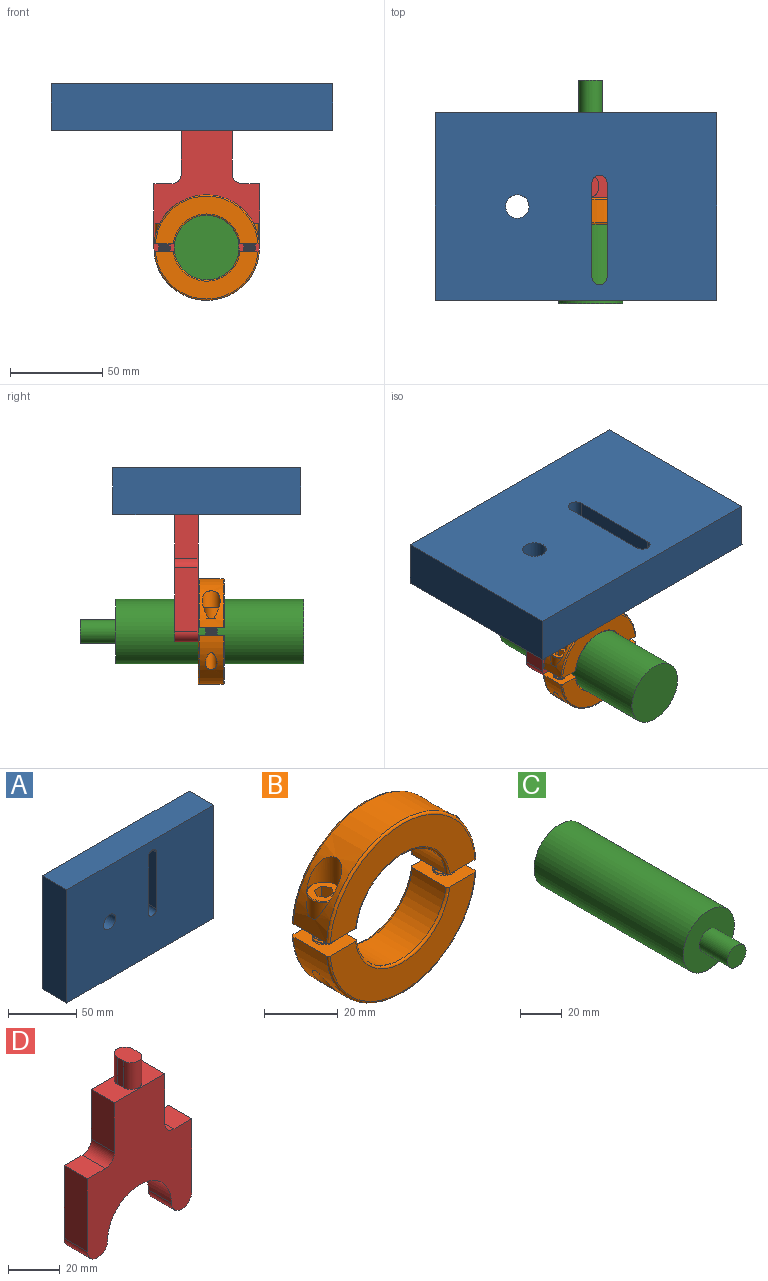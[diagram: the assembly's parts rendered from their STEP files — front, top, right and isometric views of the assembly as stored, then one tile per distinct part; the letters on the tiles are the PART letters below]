
ASSEMBLY  parts=4 mates=4
PART A: 11 faces, bbox 152.4x25.4x101.6 mm
  f0: plane 101.6x25.4mm, normal (1,0,0), area 2580.6mm2, adj f1,f3,f5,f6
  f1: plane 152.4x25.4mm, normal (0,0,1), area 3871mm2, adj f0,f2,f5,f6
  f2: plane 101.6x25.4mm, normal (-1,0,0), area 2580.6mm2, adj f1,f3,f5,f6
  f3: plane 152.4x25.4mm, normal (0,0,-1), area 3871mm2, adj f0,f2,f5,f6
  f4: cylinder r=6.35mm len=25.4mm, axis (0,1,0), area 1013.4mm2, adj f5,f6
  f5: plane 152.4x101.6mm, normal (0,-1,0), area 14884.3mm2, adj f0,f1,f2,f3,f4,f7,f8,f9
  f6: plane 152.4x101.6mm, normal (0,1,0), area 14884.3mm2, adj f0,f1,f2,f3,f4,f7,f8,f9
  f7: cylinder r=4.13mm len=25.4mm, axis (0,-1,0), area 329.4mm2, adj f5,f6,f8,f9
  f8: plane 50.8x25.4mm, normal (-1,0,0), area 1290.3mm2, adj f5,f6,f7,f10
  f9: plane 50.8x25.4mm, normal (1,0,0), area 1290.3mm2, adj f5,f6,f7,f10
  f10: cylinder r=4.13mm len=25.4mm, axis (0,-1,0), area 329.4mm2, adj f5,f6,f8,f9
PART B: 81 faces, bbox 62x14.8x62.2 mm
  f0: plane 1.42x0.05mm, normal (0,0,-1), area 0.1mm2, adj f2,f35
  f1: plane 9.02x9.02mm, normal (0,0,1), area 44.2mm2, adj f3,f4,f5,f6,f7,f8,f10
  f2: cylinder r=4.76mm len=9.53mm, axis (0,0,-1), area 182.4mm2, adj f0,f10,f11
  f3: plane 4.76x2.75mm, normal (0,1,0), area 13.1mm2, adj f1,f4,f8,f9
  f4: plane 4.76x2.38mm, normal (0.87,0.5,0), area 13.1mm2, adj f1,f3,f5,f9
  f5: plane 4.76x2.38mm, normal (0.87,-0.5,0), area 13.1mm2, adj f1,f4,f6,f9
  f6: plane 4.76x2.75mm, normal (0,-1,0), area 13.1mm2, adj f1,f5,f7,f9
  f7: plane 4.76x2.38mm, normal (-0.87,-0.5,0), area 13.1mm2, adj f1,f6,f8,f9
  f8: plane 4.76x2.38mm, normal (-0.87,0.5,0), area 13.1mm2, adj f1,f3,f7,f9
  f9: plane 5.5x4.76mm, normal (0,0,1), area 19.6mm2, adj f3,f4,f5,f6,f7,f8
  f10: cone r=4.76mm half-angle=45deg, axis (0,0,-1), area 10.5mm2, adj f1,f2
  f11: plane 9.65x9.54mm, normal (0,0,1), area 1.8mm2, adj f2,f35,f47
  f12: cylinder r=3.17mm len=6.35mm, axis (0,0,-1), area 83.1mm2, adj f38,f77,f79,f80
  f13: cylinder r=3.17mm len=13.63mm, axis (0,0,1), area 180.7mm2, adj f19,f63,f78,f79,f80
  f14: cylinder r=3.17mm len=6.35mm, axis (0,0,1), area 11.1mm2, adj f15,f20,f64,f79,f80
  f15: cylinder r=3.17mm len=6.35mm, axis (0,0,1), area 15.8mm2, adj f14,f16,f79,f80
  f16: cylinder r=3.17mm len=6.35mm, axis (0,0,1), area 15.8mm2, adj f15,f17,f79,f80
  f17: cylinder r=3.17mm len=6.35mm, axis (0,0,1), area 15.8mm2, adj f16,f18,f79,f80
  f18: cylinder r=3.17mm len=6.35mm, axis (0,0,1), area 15.8mm2, adj f17,f19,f79,f80
  f19: cylinder r=3.17mm len=6.35mm, axis (0,0,1), area 15.8mm2, adj f13,f18,f79,f80
  f20: cylinder r=3.17mm len=2.58mm, axis (0,0,1), area 0.2mm2, adj f14,f64,f80
  f21: plane 9.02x9.02mm, normal (0,0,1), area 44.2mm2, adj f24,f25,f26,f27,f28,f29,f31
  f22: cylinder r=4.76mm len=9.53mm, axis (0,0,-1), area 182.4mm2, adj f23,f31,f32
  f23: plane 1.42x0.05mm, normal (0,0,-1), area 0.1mm2, adj f22,f35
  f24: plane 4.76x2.75mm, normal (0,1,0), area 13.1mm2, adj f21,f25,f29,f30
  f25: plane 4.76x2.38mm, normal (0.87,0.5,0), area 13.1mm2, adj f21,f24,f26,f30
  f26: plane 4.76x2.38mm, normal (0.87,-0.5,0), area 13.1mm2, adj f21,f25,f27,f30
  f27: plane 4.76x2.75mm, normal (0,-1,0), area 13.1mm2, adj f21,f26,f28,f30
  f28: plane 4.76x2.38mm, normal (-0.87,-0.5,0), area 13.1mm2, adj f21,f27,f29,f30
  f29: plane 4.76x2.38mm, normal (-0.87,0.5,0), area 13.1mm2, adj f21,f24,f28,f30
  f30: plane 5.5x4.76mm, normal (0,0,1), area 19.6mm2, adj f24,f25,f26,f27,f28,f29
  f31: cone r=4.76mm half-angle=45deg, axis (0,0,-1), area 10.5mm2, adj f21,f22
  f32: plane 9.65x9.54mm, normal (0,0,1), area 1.8mm2, adj f22,f35,f46
  f33: cylinder r=3.17mm len=6.35mm, axis (0,0,-1), area 83.1mm2, adj f36,f52,f53,f54
  f34: plane 55.56x25.72mm, normal (0,1,0), area 353.2mm2, adj f36,f38,f41,f45
  f35: cylinder r=28.57mm len=56.99mm, axis (0,1,0), area 828.9mm2, adj f0,f11,f23,f32,f36,f38,f41,f42
  f36: plane 14.32x11.2mm, normal (0,0,-1), area 127.3mm2, adj f33,f34,f35,f37,f39,f40,f41,f42
  f37: cylinder r=17.46mm len=34.66mm, axis (0,1,0), area 650.2mm2, adj f36,f38,f43,f44
  f38: plane 14.32x11.2mm, normal (0,0,-1), area 127.3mm2, adj f12,f34,f35,f37,f39,f40,f41,f42
  f39: plane 55.56x25.72mm, normal (0,-1,0), area 658.7mm2, adj f36,f38,f42,f43
  f40: plane 45.46x20.69mm, normal (0,1,0), area 279.6mm2, adj f36,f38,f44,f45
  f41: torus R=27.86mm, axis (0,-1,0), area 95mm2, adj f34,f35,f36,f38
  f42: torus R=27.86mm, axis (0,-1,0), area 95mm2, adj f35,f36,f38,f39
  f43: torus R=18.18mm, axis (0,-1,0), area 57.7mm2, adj f36,f37,f38,f39
  f44: torus R=18.18mm, axis (0,-1,0), area 57.7mm2, adj f36,f37,f38,f40
  f45: torus R=23.02mm, axis (0,1,0), area 40.7mm2, adj f34,f36,f38,f40
  f46: cylinder r=4.83mm len=15.13mm, axis (0,0,-1), area 267.6mm2, adj f32,f35
  f47: cylinder r=4.83mm len=15.13mm, axis (0,0,-1), area 267.5mm2, adj f11,f35
  f48: plane 4.54x4.54mm, normal (0,0,-1), area 16.2mm2, adj f49
  f49: cone r=2.27mm half-angle=45deg, axis (0,0,1), area 14.2mm2, adj f48,f50,f53,f54,f55
  f50: cylinder r=2.59mm len=15.56mm, axis (0,0,-1), area 31.4mm2, adj f49,f52,f53,f54
  f51: cylinder r=3.17mm len=6.35mm, axis (0,0,-1), area 10.6mm2, adj f36,f53,f54,f66
  f52: plane 6.71x6.7mm, normal (0,0,-1), area 5.5mm2, adj f33,f50,f53,f54
  f53: bspline ~16.02x6.45mm, area 207.1mm2, adj f33,f49,f50,f51,f52,f55,f56,f57
  f54: bspline ~16.47x6.45mm, area 206.6mm2, adj f33,f49,f50,f51,f52,f55,f56,f57
  f55: cylinder r=3.17mm len=14.09mm, axis (0,0,-1), area 188.6mm2, adj f49,f53,f54,f60,f63
  f56: cylinder r=3.17mm len=6.35mm, axis (0,0,-1), area 15.4mm2, adj f53,f54,f57,f61,f66
  f57: cylinder r=3.17mm len=6.35mm, axis (0,0,-1), area 15.8mm2, adj f53,f54,f56,f58
  f58: cylinder r=3.17mm len=6.35mm, axis (0,0,-1), area 15.8mm2, adj f53,f54,f57,f59
  f59: cylinder r=3.17mm len=6.35mm, axis (0,0,-1), area 15.8mm2, adj f53,f54,f58,f60
  f60: cylinder r=3.17mm len=6.35mm, axis (0,0,-1), area 15.8mm2, adj f53,f54,f55,f59
  f61: cylinder r=3.17mm len=6.35mm, axis (0,0,-1), area 3.8mm2, adj f54,f56,f66
  f62: plane 55.56x25.72mm, normal (0,1,0), area 353.2mm2, adj f64,f66,f72,f73
  f63: cylinder r=28.57mm len=56.99mm, axis (0,1,0), area 988.8mm2, adj f13,f55,f64,f66,f69,f72
  f64: plane 14.32x11.2mm, normal (0,0,1), area 127.3mm2, adj f14,f20,f62,f63,f65,f67,f68,f69
  f65: cylinder r=17.46mm len=34.66mm, axis (0,1,0), area 650.2mm2, adj f64,f66,f70,f71
  f66: plane 14.32x11.2mm, normal (0,0,1), area 127.3mm2, adj f51,f56,f61,f62,f63,f65,f67,f68
  f67: plane 55.56x25.72mm, normal (0,-1,0), area 658.7mm2, adj f64,f66,f69,f70
  f68: plane 45.46x20.69mm, normal (0,1,0), area 279.6mm2, adj f64,f66,f71,f73
  f69: torus R=27.86mm, axis (0,-1,0), area 95mm2, adj f63,f64,f66,f67
  f70: torus R=18.18mm, axis (0,-1,0), area 57.7mm2, adj f64,f65,f66,f67
  f71: torus R=18.18mm, axis (0,-1,0), area 57.7mm2, adj f64,f65,f66,f68
  f72: torus R=27.86mm, axis (0,-1,0), area 95mm2, adj f62,f63,f64,f66
  f73: torus R=23.02mm, axis (0,1,0), area 40.7mm2, adj f62,f64,f66,f68
  f74: plane 4.54x4.54mm, normal (0,0,-1), area 16.2mm2, adj f78
  f75: cylinder r=2.59mm len=15.56mm, axis (0,0,-1), area 31.4mm2, adj f77,f78,f79,f80
  f76: cylinder r=3.17mm len=6.35mm, axis (0,0,-1), area 10.6mm2, adj f38,f64,f79,f80
  f77: plane 6.71x6.7mm, normal (0,0,-1), area 5.5mm2, adj f12,f75,f79,f80
  f78: cone r=2.27mm half-angle=45deg, axis (0,0,1), area 14.2mm2, adj f13,f74,f75,f79,f80
  f79: bspline ~16.02x6.45mm, area 207.1mm2, adj f12,f13,f14,f15,f16,f17,f18,f19
  f80: bspline ~16.47x6.45mm, area 206.6mm2, adj f12,f13,f14,f15,f16,f17,f18,f19
PART C: 5 faces, bbox 34.9x120.7x34.9 mm
  f0: cylinder r=17.46mm len=101.6mm, axis (0,1,0), area 11147.6mm2, adj f1,f3
  f1: plane 34.93x34.93mm, normal (0,1,0), area 958mm2, adj f0
  f2: cylinder r=6.35mm len=19.05mm, axis (0,-1,0), area 760.1mm2, adj f3,f4
  f3: plane 34.93x34.93mm, normal (0,-1,0), area 831.3mm2, adj f0,f2
  f4: plane 12.7x12.7mm, normal (0,-1,0), area 126.7mm2, adj f2
PART D: 19 faces, bbox 57.2x12.7x81.5 mm
  f0: plane 68.84x57.15mm, normal (0,1,0), area 2396.2mm2, adj f1,f2,f3,f4,f5,f6,f7,f8
  f1: cylinder r=5.56mm len=12.7mm, axis (0,1,0), area 221.7mm2, adj f0,f2,f9,f10
  f2: plane 34.6x12.7mm, normal (1,0,0), area 439.4mm2, adj f0,f1,f3,f10
  f3: plane 12.7x9.73mm, normal (0,0,1), area 123.5mm2, adj f0,f2,f10,f11
  f4: plane 23.61x12.7mm, normal (1,0,0), area 299.9mm2, adj f0,f10,f11,f13
  f5: plane 23.61x12.7mm, normal (-1,0,0), area 299.9mm2, adj f0,f10,f12,f13
  f6: plane 12.7x9.73mm, normal (0,0,1), area 123.5mm2, adj f0,f7,f10,f12
  f7: plane 34.6x12.7mm, normal (-1,0,0), area 439.4mm2, adj f0,f6,f8,f10
  f8: cylinder r=5.56mm len=12.7mm, axis (0,1,0), area 221.7mm2, adj f0,f7,f9,f10
  f9: cylinder r=17.46mm len=34.93mm, axis (0,1,0), area 696.7mm2, adj f0,f1,f8,f10
  f10: plane 68.84x57.15mm, normal (0,-1,0), area 2396.2mm2, adj f1,f2,f3,f4,f5,f6,f7,f8
  f11: cylinder r=5.08mm len=12.7mm, axis (0,-1,0), area 101.3mm2, adj f0,f3,f4,f10
  f12: cylinder r=5.08mm len=12.7mm, axis (0,-1,0), area 101.3mm2, adj f0,f5,f6,f10
  f13: plane 27.53x12.7mm, normal (0,0,1), area 270mm2, adj f0,f4,f5,f10,f14,f15,f16,f17
  f14: plane 12.7x3.18mm, normal (-1,0,0), area 40.3mm2, adj f13,f15,f17,f18
  f15: cylinder r=4.13mm len=12.7mm, axis (0,0,-1), area 164.7mm2, adj f13,f14,f16,f18
  f16: plane 12.7x3.18mm, normal (1,0,0), area 40.3mm2, adj f13,f15,f17,f18
  f17: cylinder r=4.13mm len=12.7mm, axis (0,0,-1), area 164.7mm2, adj f13,f14,f16,f18
  f18: plane 11.43x8.26mm, normal (0,0,1), area 79.7mm2, adj f14,f15,f16,f17
PLACE A rot(axis=(1,0,0),90deg) t=(211.74,88.38,99.65)mm fixed
PLACE B t=(219.7,86,10.96)mm
PLACE C rot(axis=(0.71,0,-0.71),180deg) t=(219.7,36.06,10.96)mm
PLACE D t=(219.7,105.84,10.96)mm
MATE parallel C.f0 <-> A.f1  axis (0,-1,0) through (219.7,36.06,10.96)mm
MATE cylindrical C.f0 <-> B.f35  axis (0,-1,0) through (219.7,86.86,10.96)mm
MATE pin_slot A.f10 <-> D.f17  axis (0,0,-1) through (224.44,101.08,74.25)mm
MATE fastened B.f35 <-> D.f9  axis (0,1,0) through (219.7,93.14,10.96)mm
